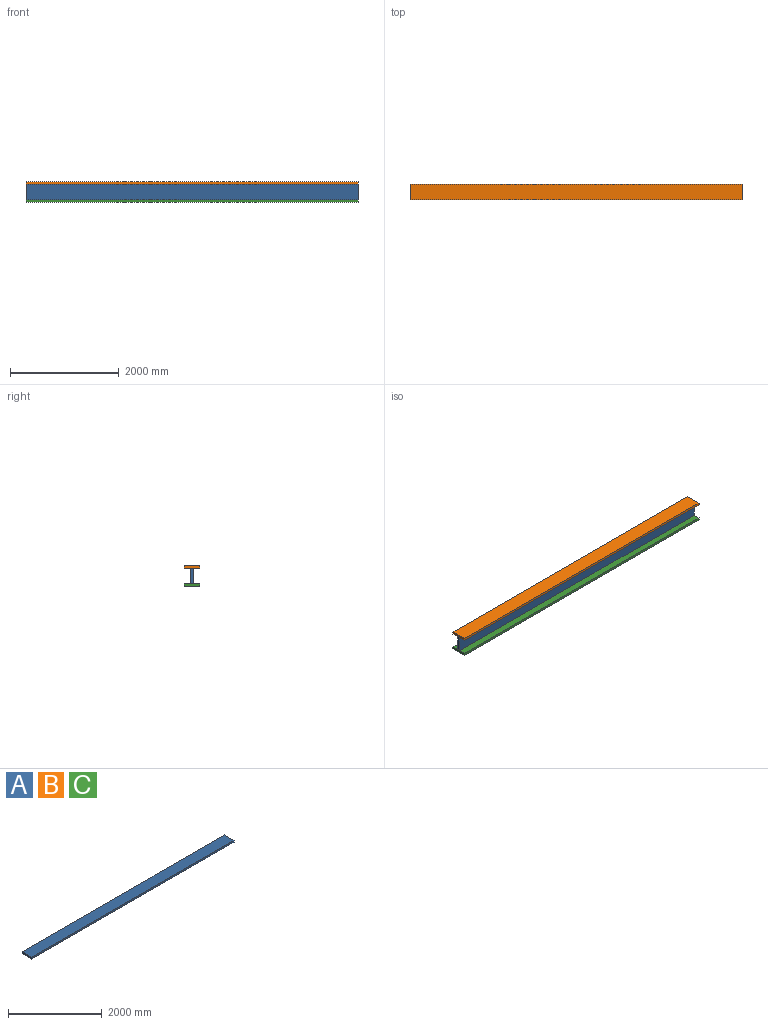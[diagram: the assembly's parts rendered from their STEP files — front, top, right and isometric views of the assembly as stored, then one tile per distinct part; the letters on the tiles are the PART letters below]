
ASSEMBLY  parts=3 mates=2
PART A: 6 faces, bbox 6096x292.1x44.5 mm
  f0: plane 6096x292.1mm, normal (0,0,-1), area 1780641.6mm2, adj f1,f3,f4,f5
  f1: plane 6096x44.45mm, normal (0,1,0), area 270967.2mm2, adj f0,f2,f4,f5
  f2: plane 6096x292.1mm, normal (0,0,1), area 1780641.6mm2, adj f1,f3,f4,f5
  f3: plane 6096x44.45mm, normal (0,-1,0), area 270967.2mm2, adj f0,f2,f4,f5
  f4: plane 292.1x44.45mm, normal (1,0,0), area 12983.8mm2, adj f0,f1,f2,f3
  f5: plane 292.1x44.45mm, normal (-1,0,0), area 12983.8mm2, adj f0,f1,f2,f3
PART B: same geometry as A
PART C: same geometry as A
PLACE A rot(axis=(1,0,0),90deg) t=(0,168.27,336.55)mm
PLACE B t=(0,0,336.55)mm
PLACE C at identity fixed
MATE fastened A.f3 <-> C.f2  axis (0,0,-1) through (0,0,190.5)mm
MATE fastened A.f1 <-> B.f0  axis (0,0,1) through (0,0,482.6)mm
